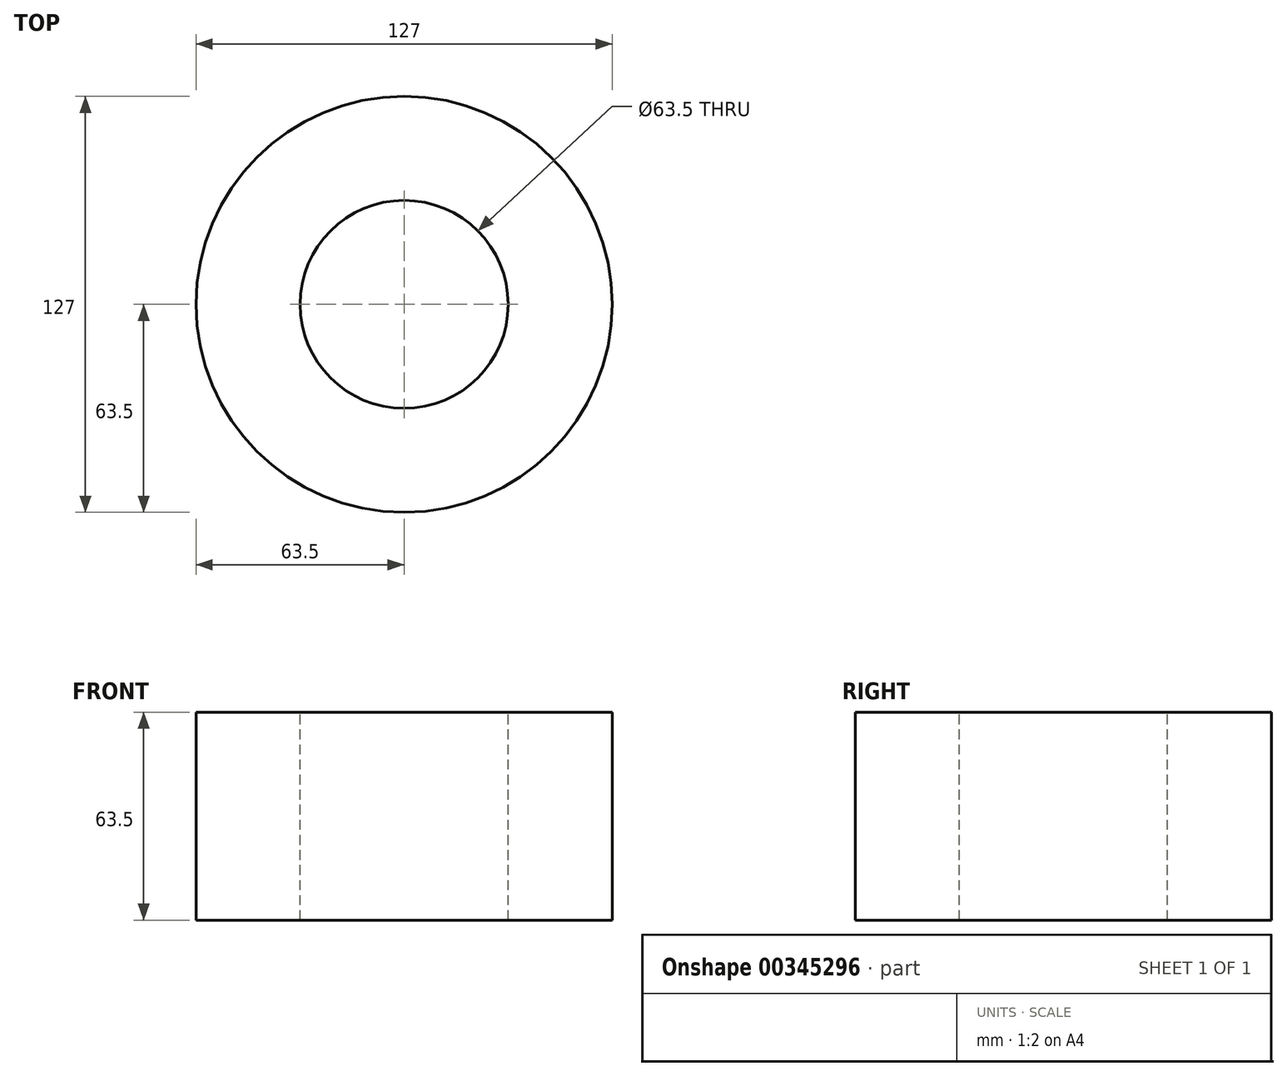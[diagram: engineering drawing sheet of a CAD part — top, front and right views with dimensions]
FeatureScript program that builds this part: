
annotation { "Feature Type Name" : "Feature", "Feature Type Description" : "" }
export const myFeature = defineFeature(function(context is Context, id is Id, definition is map)
    precondition{}
    {
        {
            var Q0;
            Q0=qCreatedBy(makeId("Top.planeOp"),FACE);
            var sketch = newSketch(context, id + "F0", { "sketchPlane" : qUnion([Q0])});
            skCircle(sketch, "E0", {"center": v(0, 0) * mm, "radius": 63.5 * mm});
            skSolve(sketch);
        }
        {
            var Q0;
            Q0 = qSketchRegion(id + "F0", true);
            extrude(context, id + "F1", {"entities" : qUnion([Q0]), "depth" : 63.5 * mm});
        }
        {
            var Q0;
            Q0=makeQuery(id+"F1.opExtrude","CAP_FACE",FACE,{"disambiguationData":[OSD([sQuery(id+"F0.wireOp",EDGE,"E0")])],"isStart":false});
            var sketch = newSketch(context, id + "F2", { "sketchPlane" : qUnion([Q0])});
            skCircle(sketch, "E1", {"center": v(0, 0) * mm, "radius": 31.75 * mm});
            skSolve(sketch);
        }
        {
            var Q0;
            Q0=makeQuery(id+"F2.imprint","IMPRINT",FACE,{"disambiguationData":[TD([[makeQuery(id+"F2.imprint","IMPRINT",EDGE,{"derivedFrom":sQuery(id+"F2.wireOp",EDGE,"E1")}),1.0]])]});
            var Q1;
            Q1=makeQuery(id+"F1.opExtrude","CAP_FACE",FACE,{"disambiguationData":[OSD([sQuery(id+"F0.wireOp",EDGE,"E0")])],"isStart":true});
            extrude(context, id + "F3", {"entities" : qUnion([Q0]), "operationType" : NewBodyOperationType.REMOVE, "endBound" : BoundingType.UP_TO_SURFACE, "oppositeDirection" : true, "endBoundEntityFace" : qUnion([Q1]), "depth" : 63.5 * mm});
        }
    });
